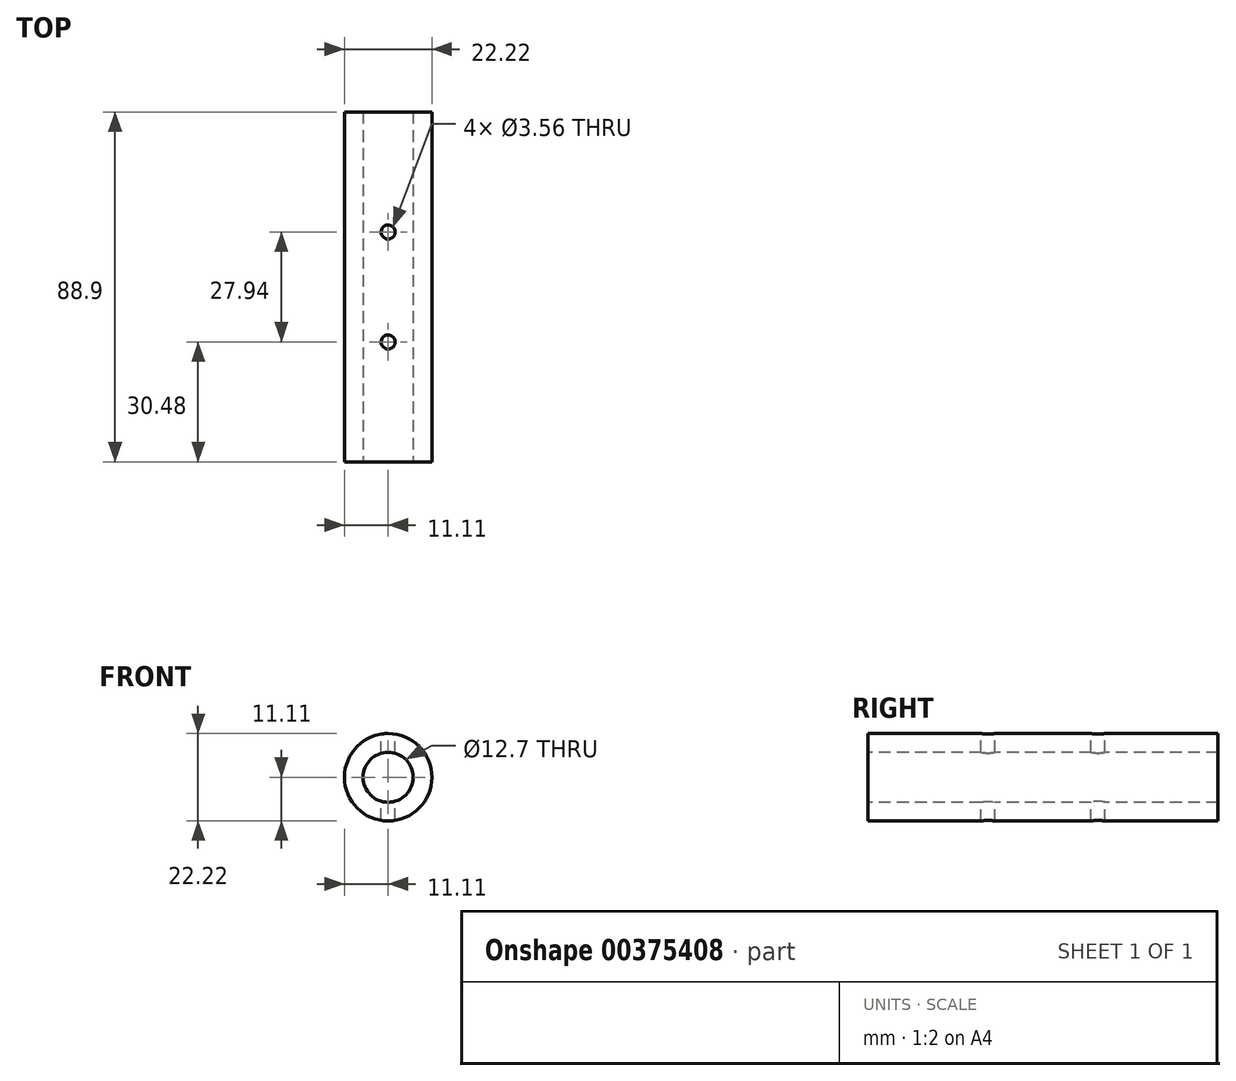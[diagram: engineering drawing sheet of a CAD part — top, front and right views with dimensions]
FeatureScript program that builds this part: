
annotation { "Feature Type Name" : "Feature", "Feature Type Description" : "" }
export const myFeature = defineFeature(function(context is Context, id is Id, definition is map)
    precondition{}
    {
        {
            var Q0;
            Q0=qCreatedBy(makeId("Front.planeOp"),FACE);
            var sketch = newSketch(context, id + "F0", { "sketchPlane" : qUnion([Q0])});
            skCircle(sketch, "E0", {"center": v(0, 0) * mm, "radius": 11.11 * mm});
            skSolve(sketch);
        }
        {
            var Q0;
            Q0=qSketchRegion(id+"F0",true);
            extrude(context, id + "F1", {"entities" : qUnion([Q0]), "depth" : 88.9 * mm, "symmetric" : true});
        }
        {
            var Q0;
            Q0=makeQuery(id+"F1.opExtrude","CAP_FACE",FACE,{"disambiguationData":[OSD([sQuery(id+"F0.wireOp",EDGE,"E0")])],"isStart":false});
            var sketch = newSketch(context, id + "F2", { "sketchPlane" : qUnion([Q0])});
            skCircle(sketch, "E1", {"center": v(0, 0) * mm, "radius": 6.35 * mm});
            skSolve(sketch);
        }
        {
            var Q0;
            Q0=qSketchRegion(id+"F2",true);
            extrude(context, id + "F3", {"entities" : qUnion([Q0]), "operationType" : NewBodyOperationType.REMOVE, "endBound" : BoundingType.THROUGH_ALL, "oppositeDirection" : true, "depth" : 25.4 * mm});
        }
        {
            var Q0;
            Q0=qCreatedBy(makeId("Top.planeOp"),FACE);
            var sketch = newSketch(context, id + "F4", { "sketchPlane" : qUnion([Q0])});
            skLineSegment(sketch, "E2.0", {"start": v(11.11, 44.45) * mm, "end": v(-11.11, 44.45) * mm});
            skLineSegment(sketch, "E3", {"start": v(0, 0) * mm, "end": v(0, 13.97) * mm, "construction": true});
            skCircle(sketch, "E4", {"center": v(0, 13.97) * mm, "radius": 1.78 * mm});
            skSolve(sketch);
        }
        {
            var Q0;
            Q0=qSketchRegion(id+"F4",true);
            extrude(context, id + "F5", {"entities" : qUnion([Q0]), "operationType" : NewBodyOperationType.REMOVE, "oppositeDirection" : true, "depth" : 22.22 * mm, "symmetric" : true});
        }
        {
            var Q0;
            Q0=qCreatedBy(makeId("Top.planeOp"),FACE);
            var sketch = newSketch(context, id + "F6", { "sketchPlane" : qUnion([Q0])});
            skLineSegment(sketch, "E5", {"start": v(0, 0) * mm, "end": v(0, -13.97) * mm, "construction": true});
            skCircle(sketch, "E6", {"center": v(0, -13.97) * mm, "radius": 1.78 * mm});
            skSolve(sketch);
        }
        {
            var Q0;
            Q0=qSketchRegion(id+"F6",true);
            extrude(context, id + "F7", {"entities" : qUnion([Q0]), "operationType" : NewBodyOperationType.REMOVE, "oppositeDirection" : true, "depth" : 22.22 * mm, "symmetric" : true});
        }
    });
